# Revit family: NAU_Naughtone_Stng_Ever
name_source: partatom
category: Furniture
revit_build: Autodesk Revit 2018 (Build: 20170223_1515(x64)
units: mm (PartAtom-declared; Revit-internal decimal feet)

## family parameters
Always vertical = Yes
Cut with Voids When Loaded = No
OmniClass Number = 23.40.20.00
OmniClass Title = General Furniture and Specialties
Room Calculation Point = No
Shared = Yes
Work Plane-Based = No

## types (6) — shared parameters
Assembly Code = E2020200
AssetType = Movable
BIMObjectName = NAU_Naughtone_Seating_Ever
Category = Pr_40_50_12 : Chairs, seats and benches
Color = Grey
DurationUnit = year
FootMaterial = Rubber-Black-Matte
IfcExportAs = IfcFurnishingElementType
IfcExportType = CHAIR
Keynote = Pr_40_50_12
MainColor = Grey
ManufacturerAddress = Knaresborough Tech Park, Manse Lane, Knaresborough, HG5 8LF
ManufacturerName = Naughtone
ManufacturerURL = www.naughtone.com
NBSDescription = Seating
NBSReference = 45-35-72/352
Name = Seating_Ever_Naughtone
NominalHeight = 760 mm
NominalWidth = 800 mm  [stored 2.62467 ft]
ProductInformation = www.naughtone.com/products/
Revision = 1
Shape = Rectangular
URL = www.naughtone.com
Uniclass2015Code = Pr_40_50_12
Uniclass2015Title = Chairs, seats and benches
Version = 1
WarrantyDescription = Request warranty information from naughtone
WarrantyDurationLabor = 7
WarrantyDurationParts = 7
WarrantyDurationUnit = year

## per-type parameters (varying)
| type | Description | Finish | IsMetalLeg | IsWoodLeg | Material | Model | ModelNumber | ModelReference | NominalLength | Offset1 | Offset2 | Size |
| Ever Chair - Steel Legs - EVER12AST | Ever Chair - Steel Legs | Fabric upholstery. Black, white or RAL steel base. | Yes | No | Shell and seat in upholstered foam. Steel legs | EVER12AST | EVER12AST | Ever Chair - Steel Legs | 1105 mm  [stored 3.62533 ft] | 1000 mm  [stored 3.28084 ft] | 1000 mm  [stored 3.28084 ft] | 1105 x 800 x 760mm |
| Ever Chair - Wood Legs - EVER12AWD | Ever Chair - Wood Legs | Fabric upholstery. Oak or Walnut solid wood base. | No | Yes | Shell and seat in upholstered foam. Solid wood legs with steel sub-frame | EVER12AWD | EVER12AWD | Ever Chair - Wood Legs | 1105 mm  [stored 3.62533 ft] | 1000 mm  [stored 3.28084 ft] | 1000 mm  [stored 3.28084 ft] | 1105 x 800 x 760mm |
| Ever 2 Seat Sofa - Steel Legs - EVER22AST | Ever 2 Seat Sofa - Steel Legs | Fabric upholstery. Black, white or RAL steel base. | Yes | No | Shell and seat in upholstered foam. Steel legs | EVER22AST | EVER22AST | Ever 2 Seat Sofa - Steel Legs | 1695 mm | 0 mm  [stored 0 ft] | 1000 mm  [stored 3.28084 ft] | 1695 x 800 x 760mm |
| Ever 2 Seat Sofa - Wood Legs - EVER22AWD | Ever 2 Seat Sofa - Wood Legs | Fabric upholstery. Oak or Walnut solid wood base. | No | Yes | Shell and seat in upholstered foam. Solid wood legs with steel sub-frame | EVER22AWD | EVER22AWD | Ever 2 Seat Sofa - Wood Legs | 1695 mm | 0 mm  [stored 0 ft] | 1000 mm  [stored 3.28084 ft] | 1695 x 800 x 760mm |
| Ever 3 Seat Sofa - Steel Legs - EVER32AST | Ever 3 Seat Sofa - Steel Legs | Fabric upholstery. Black, white or RAL steel base. | Yes | No | Shell and seat in upholstered foam. Steel legs | EVER32AST | EVER32AST | Ever 3 Seat Sofa - Steel Legs | 2325 mm | 315 mm  [stored 1.03346 ft] | 315 mm  [stored 1.03346 ft] | 2325 x 800 x 760mm |
| Ever 3 Seat Sofa - Wood Legs - EVER32AWD | Ever 3 Seat Sofa - Wood Legs | Fabric upholstery. Oak or Walnut solid wood base. | No | Yes | Shell and seat in upholstered foam. Solid wood legs with steel sub-frame | EVER32AWD | EVER32AWD | Ever 3 Seat Sofa - Wood Legs | 2325 mm | 315 mm  [stored 1.03346 ft] | 315 mm  [stored 1.03346 ft] | 2325 x 800 x 760mm |

note: [stored X ft] marks values corroborated as IEEE doubles in the binary element streams (Revit-internal decimal feet)

## geometry (parser evidence)
native form markers: Sweep x5
no freeform markers — native parametric forms only
